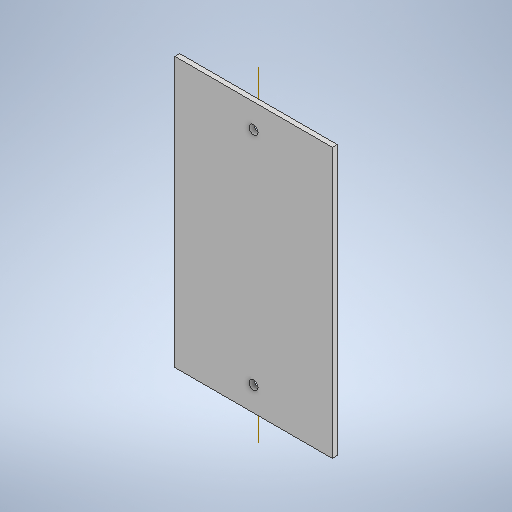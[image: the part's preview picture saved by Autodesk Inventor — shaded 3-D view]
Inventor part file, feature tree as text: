
AUTODESK INVENTOR PART (.ipt)
format: ipt  version: 2025 (Build 290162000, 162)  size: 242,176 bytes
history: native  units: in
note: dims shown in document units (in); Inventor stores cm internally (conversion verified against a paired STEP export)
features: sketch x3, extrude x2, other x1
ambient origin geometry x8: Origin, YZ Plane, XZ Plane, XY Plane, X Axis, Y Axis, Z Axis, Center Point
bodies: Body1 (feature_tree)
feature tree (6):
  other  "솔리드1"
  sketch  "스케치1"
  extrude  "돌출1"  Depth=2.0472in
  extrude  "돌출2"  Depth=3.5039in
  sketch  "스케치2"
  sketch  "스케치3"
